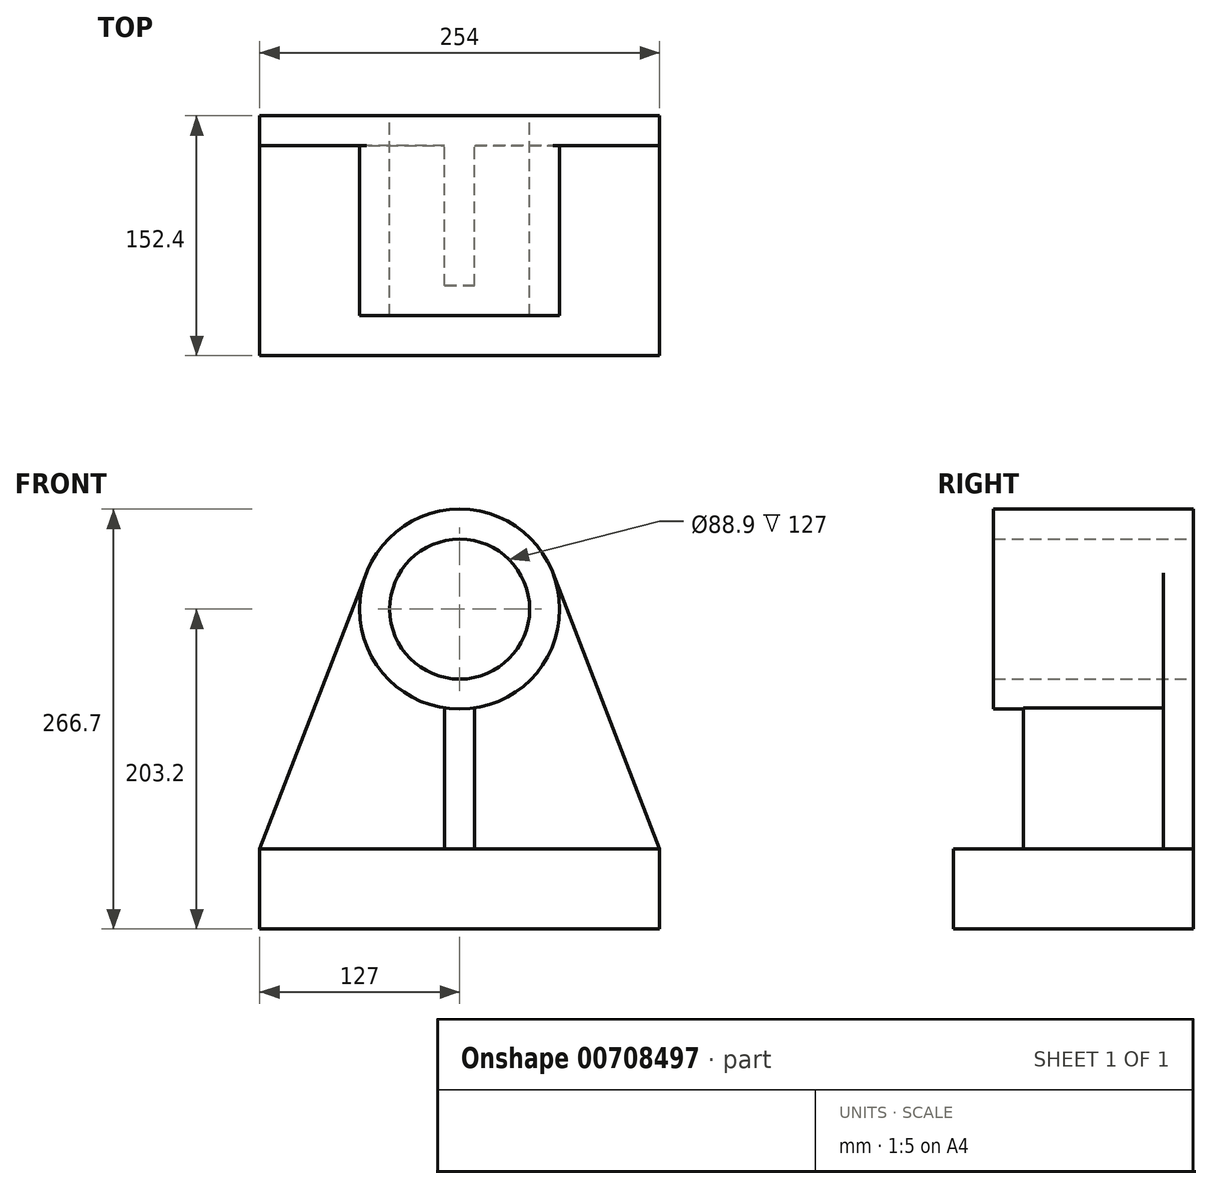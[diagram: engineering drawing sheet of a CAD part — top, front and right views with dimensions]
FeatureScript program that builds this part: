
annotation { "Feature Type Name" : "Feature", "Feature Type Description" : "" }
export const myFeature = defineFeature(function(context is Context, id is Id, definition is map)
    precondition{}
    {
        {
            var Q0;
            Q0=qCreatedBy(makeId("Front.planeOp"),FACE);
            var sketch = newSketch(context, id + "F0", { "sketchPlane" : qUnion([Q0])});
            skLineSegment(sketch, "E0.bottom", {"start": v(0, 0) * mm, "end": v(254, 0) * mm});
            skLineSegment(sketch, "E0.top", {"start": v(0, -50.8) * mm, "end": v(254, -50.8) * mm});
            skLineSegment(sketch, "E0.left", {"start": v(0, 0) * mm, "end": v(0, -50.8) * mm});
            skLineSegment(sketch, "E0.right", {"start": v(254, 0) * mm, "end": v(254, -50.8) * mm});
            skSolve(sketch);
        }
        {
            var Q0;
            Q0 = qSketchRegion(id + "F0", true);
            extrude(context, id + "F1", {"entities" : qUnion([Q0]), "oppositeDirection" : true, "depth" : 152.4 * mm, "offsetDistance" : 25.4 * mm});
        }
        {
            var Q0;
            Q0=makeQuery(id+"F1.opExtrude","CAP_FACE",FACE,{"disambiguationData":[OSD([sQuery(id+"F0.wireOp",EDGE,"E0.bottom"),sQuery(id+"F0.wireOp",EDGE,"E0.top"),sQuery(id+"F0.wireOp",EDGE,"E0.left"),sQuery(id+"F0.wireOp",EDGE,"E0.right")])],"isStart":false});
            var sketch = newSketch(context, id + "F2", { "sketchPlane" : qUnion([Q0])});
            skCircle(sketch, "E1", {"center": v(-127, 152.4) * mm, "radius": 63.5 * mm});
            skCircle(sketch, "E2", {"center": v(-127, 152.4) * mm, "radius": 44.45 * mm});
            skLineSegment(sketch, "E3", {"start": v(-117.48, 89.62) * mm, "end": v(-117.48, 0) * mm});
            skLineSegment(sketch, "E4", {"start": v(-117.48, 0) * mm, "end": v(-136.53, 0) * mm});
            skLineSegment(sketch, "E5", {"start": v(-136.53, 0) * mm, "end": v(-136.53, 89.62) * mm});
            skLineSegment(sketch, "E6", {"start": v(-67.77, 175.3) * mm, "end": v(0, 0) * mm});
            skLineSegment(sketch, "E7", {"start": v(-186.23, 175.3) * mm, "end": v(-254, 0) * mm});
            skSolve(sketch);
        }
        {
            var Q0;
            {var subQ0=sQuery(id+"F2.wireOp",EDGE,"E3");Q0=makeQuery(id+"F2.imprint","IMPRINT",FACE,{"disambiguationData":[TD([[makeQuery(id+"F2.imprint","IMPRINT",EDGE,{"derivedFrom":subQ0}),-1.0]])]});}
            extrude(context, id + "F3", {"entities" : qUnion([Q0]), "operationType" : NewBodyOperationType.ADD, "oppositeDirection" : true, "depth" : 107.95 * mm, "offsetDistance" : 25.4 * mm});
        }
        {
            var Q0;
            Q0=makeQuery(id+"F2.imprint","IMPRINT",FACE,{"disambiguationData":[TD([[makeQuery(id+"F2.imprint","IMPRINT",EDGE,{"derivedFrom":sQuery(id+"F2.wireOp",EDGE,"E2")}),-1.0]])]});
            extrude(context, id + "F4", {"entities" : qUnion([Q0]), "operationType" : NewBodyOperationType.ADD, "oppositeDirection" : true, "depth" : 127 * mm, "offsetDistance" : 25.4 * mm});
        }
        {
            var Q0;
            {var subQ0=sQuery(id+"F2.wireOp",EDGE,"E5");Q0=makeQuery(id+"F2.imprint","IMPRINT",FACE,{"disambiguationData":[TD([[makeQuery(id+"F2.imprint","IMPRINT",EDGE,{"derivedFrom":subQ0}),1.0]])]});}
            var Q1;
            {var subQ0=sQuery(id+"F2.wireOp",EDGE,"E3");Q1=makeQuery(id+"F2.imprint","IMPRINT",FACE,{"disambiguationData":[TD([[makeQuery(id+"F2.imprint","IMPRINT",EDGE,{"derivedFrom":subQ0}),1.0]])]});}
            extrude(context, id + "F5", {"entities" : qUnion([Q0, Q1]), "operationType" : NewBodyOperationType.ADD, "oppositeDirection" : true, "depth" : 19.05 * mm, "offsetDistance" : 25.4 * mm});
        }
    });
